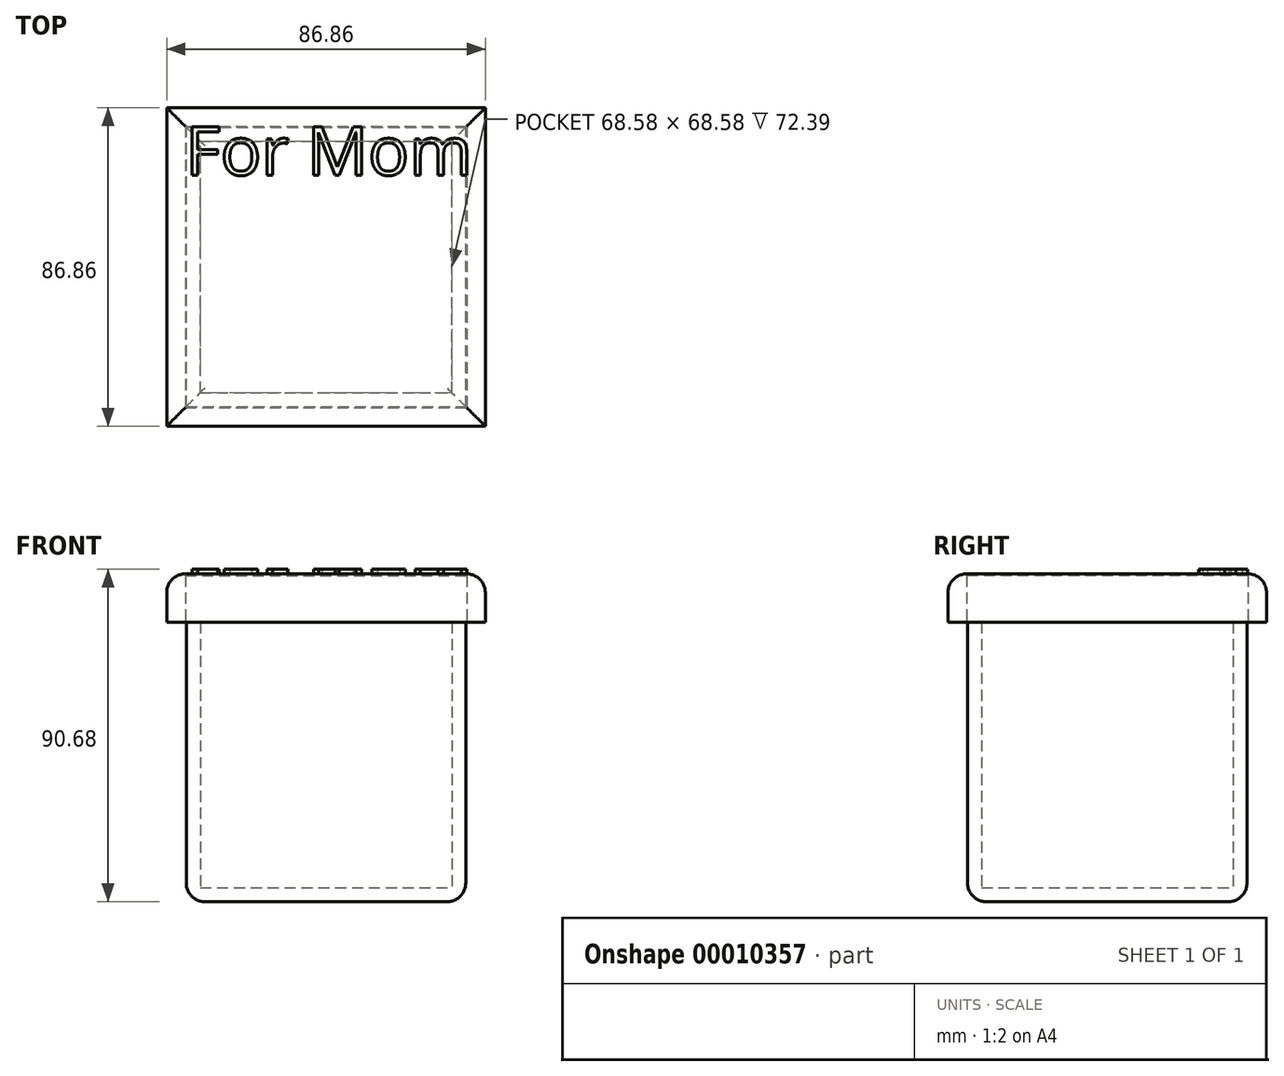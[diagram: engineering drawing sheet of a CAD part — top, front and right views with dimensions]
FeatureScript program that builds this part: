
annotation { "Feature Type Name" : "Feature", "Feature Type Description" : "" }
export const myFeature = defineFeature(function(context is Context, id is Id, definition is map)
    precondition{}
    {
        {
            var Q0;
            Q0=qCreatedBy(makeId("Front.planeOp"),FACE);
            var sketch = newSketch(context, id + "F0", { "sketchPlane" : qUnion([Q0])});
            skLineSegment(sketch, "E0.bottom", {"start": v(-76.2, 0) * mm, "end": v(0, 0) * mm});
            skLineSegment(sketch, "E0.top", {"start": v(-76.2, -76.2) * mm, "end": v(0, -76.2) * mm});
            skLineSegment(sketch, "E0.left", {"start": v(-76.2, 0) * mm, "end": v(-76.2, -76.2) * mm});
            skLineSegment(sketch, "E0.right", {"start": v(0, 0) * mm, "end": v(0, -76.2) * mm});
            skSolve(sketch);
        }
        {
            var Q0;
            Q0=makeQuery(id+"F0.imprint","IMPRINT",FACE,{"disambiguationData":[TD([[makeQuery(id+"F0.imprint","IMPRINT",EDGE,{"derivedFrom":sQuery(id+"F0.wireOp",EDGE,"E0.bottom")}),-1.0]])]});
            extrude(context, id + "F1", {"entities" : qUnion([Q0]), "depth" : 76.2 * mm});
        }
        {
            var Q0;
            Q0=makeQuery(id+"F1.opExtrude","SWEPT_FACE",FACE,{"disambiguationData":[OSD([sQuery(id+"F0.wireOp",EDGE,"E0.bottom")])]});
            shell(context, id + "F2", {"entities" : qUnion([Q0]), "thickness" : 3.8 * mm});
        }
        {
            var Q0;
            Q0=qCreatedBy(makeId("Top.planeOp"),FACE);
            var sketch = newSketch(context, id + "F3", { "sketchPlane" : qUnion([Q0])});
            skLineSegment(sketch, "E1.bottom", {"start": v(-76.2, 0) * mm, "end": v(0, 0) * mm});
            skLineSegment(sketch, "E1.top", {"start": v(-76.2, -76.2) * mm, "end": v(0, -76.2) * mm});
            skLineSegment(sketch, "E1.left", {"start": v(-76.2, 0) * mm, "end": v(-76.2, -76.2) * mm});
            skLineSegment(sketch, "E1.right", {"start": v(0, 0) * mm, "end": v(0, -76.2) * mm});
            skLineSegment(sketch, "E2.0", {"start": v(-76.45, 0.25) * mm, "end": v(0.25, 0.25) * mm});
            skLineSegment(sketch, "E2.1", {"start": v(-76.45, 0.25) * mm, "end": v(-76.45, -76.45) * mm});
            skLineSegment(sketch, "E2.2", {"start": v(-76.45, -76.45) * mm, "end": v(0.25, -76.45) * mm});
            skLineSegment(sketch, "E2.3", {"start": v(0.25, 0.25) * mm, "end": v(0.25, -76.45) * mm});
            skLineSegment(sketch, "E3.0", {"start": v(-81.53, 5.33) * mm, "end": v(5.33, 5.33) * mm});
            skLineSegment(sketch, "E3.1", {"start": v(-81.53, 5.33) * mm, "end": v(-81.53, -81.53) * mm});
            skLineSegment(sketch, "E3.2", {"start": v(-81.53, -81.53) * mm, "end": v(5.33, -81.53) * mm});
            skLineSegment(sketch, "E3.3", {"start": v(5.33, 5.33) * mm, "end": v(5.33, -81.53) * mm});
            skSolve(sketch);
        }
        {
            var Q0;
            Q0=makeQuery(id+"F3.imprint","IMPRINT",FACE,{"disambiguationData":[TD([[makeQuery(id+"F3.imprint","IMPRINT",EDGE,{"derivedFrom":sQuery(id+"F3.wireOp",EDGE,"E2.0")}),1.0]])]});
            extrude(context, id + "F4", {"entities" : qUnion([Q0]), "depth" : 12.7 * mm});
        }
        {
            var Q0;
            Q0=makeQuery(id+"F4.opExtrude","CAP_FACE",FACE,{"disambiguationData":[OSD([sQuery(id+"F3.wireOp",EDGE,"E2.0"),sQuery(id+"F3.wireOp",EDGE,"E2.1"),sQuery(id+"F3.wireOp",EDGE,"E2.2"),sQuery(id+"F3.wireOp",EDGE,"E2.3"),sQuery(id+"F3.wireOp",EDGE,"E3.0"),sQuery(id+"F3.wireOp",EDGE,"E3.1"),sQuery(id+"F3.wireOp",EDGE,"E3.2"),sQuery(id+"F3.wireOp",EDGE,"E3.3")])],"isStart":false});
            var sketch = newSketch(context, id + "F5", { "sketchPlane" : qUnion([Q0])});
            skLineSegment(sketch, "E4.bottom", {"start": v(-81.53, 5.33) * mm, "end": v(5.33, 5.33) * mm});
            skLineSegment(sketch, "E4.top", {"start": v(-81.53, -81.53) * mm, "end": v(5.33, -81.53) * mm});
            skLineSegment(sketch, "E4.left", {"start": v(-81.53, 5.33) * mm, "end": v(-81.53, -81.53) * mm});
            skLineSegment(sketch, "E4.right", {"start": v(5.33, 5.33) * mm, "end": v(5.33, -81.53) * mm});
            skSolve(sketch);
        }
        {
            var Q0;
            Q0 = qSketchRegion(id + "F5", true);
            extrude(context, id + "F6", {"entities" : qUnion([Q0]), "operationType" : NewBodyOperationType.ADD, "depth" : 0.5 * mm});
        }
        {
            var Q0;
            Q0=makeQuery(id+"F6.opExtrude","CAP_EDGE",EDGE,{"disambiguationData":[OSD([sQuery(id+"F5.wireOp",EDGE,"E4.top")])],"isStart":false});
            var Q1;
            Q1=makeQuery(id+"F6.opExtrude","CAP_EDGE",EDGE,{"disambiguationData":[OSD([sQuery(id+"F5.wireOp",EDGE,"E4.left")])],"isStart":false});
            var Q2;
            Q2=makeQuery(id+"F6.opExtrude","CAP_EDGE",EDGE,{"disambiguationData":[OSD([sQuery(id+"F5.wireOp",EDGE,"E4.right")])],"isStart":false});
            var Q3;
            Q3=makeQuery(id+"F6.opExtrude","CAP_EDGE",EDGE,{"disambiguationData":[OSD([sQuery(id+"F5.wireOp",EDGE,"E4.bottom")])],"isStart":false});
            fillet(context, id + "F7", {"entities" : qUnion([Q0, Q1, Q2, Q3]), "radius" : 5.08 * mm, "tangentPropagation" : true, "allowEdgeOverflow" : false});
        }
        {
            var Q0;
            Q0=makeQuery(id+"F1.opExtrude","SWEPT_EDGE",EDGE,{"disambiguationData":[OSD([sQuery(id+"F0.wireOp",EDGE,"E0.top"),sQuery(id+"F0.wireOp",EDGE,"E0.left")])]});
            var Q1;
            Q1=makeQuery(id+"F1.opExtrude","CAP_EDGE",EDGE,{"disambiguationData":[OSD([sQuery(id+"F0.wireOp",EDGE,"E0.top")])],"isStart":false});
            var Q2;
            Q2=makeQuery(id+"F1.opExtrude","SWEPT_EDGE",EDGE,{"disambiguationData":[OSD([sQuery(id+"F0.wireOp",EDGE,"E0.top"),sQuery(id+"F0.wireOp",EDGE,"E0.right")])]});
            var Q3;
            Q3=makeQuery(id+"F1.opExtrude","CAP_EDGE",EDGE,{"disambiguationData":[OSD([sQuery(id+"F0.wireOp",EDGE,"E0.top")])],"isStart":true});
            fillet(context, id + "F8", {"entities" : qUnion([Q0, Q1, Q2, Q3]), "radius" : 5.08 * mm, "tangentPropagation" : true, "allowEdgeOverflow" : false});
        }
        {
            var Q0;
            Q0=makeQuery(id+"F6.opExtrude","CAP_FACE",FACE,{"disambiguationData":[OSD([sQuery(id+"F5.wireOp",EDGE,"E4.bottom"),sQuery(id+"F5.wireOp",EDGE,"E4.top"),sQuery(id+"F5.wireOp",EDGE,"E4.left"),sQuery(id+"F5.wireOp",EDGE,"E4.right")])],"isStart":false});
            var sketch = newSketch(context, id + "F9", { "sketchPlane" : qUnion([Q0])});
            skText(sketch, "E5", { "text": "For Mom", "fontName": "OpenSans-Regular.ttf"});
            const initialGuessF9  = {"E5": [-0.07645, -0.01307, 1, 0, 0.01333]};
            skSetInitialGuess(sketch, initialGuessF9);
            skSolve(sketch);
        }
        {
            var Q0;
            Q0=makeQuery(id+"F9.imprint","IMPRINT",FACE,{"disambiguationData":[TD([[makeQuery(id+"F9.imprint","IMPRINT",EDGE,{"derivedFrom":sQuery(id+"F9.wireOp",EDGE,"E5.sketch_text.stroke-0")}),-1.0]])]});
            var Q1;
            Q1=makeQuery(id+"F9.imprint","IMPRINT",FACE,{"disambiguationData":[TD([[makeQuery(id+"F9.imprint","IMPRINT",EDGE,{"derivedFrom":sQuery(id+"F9.wireOp",EDGE,"E5.sketch_text.stroke-10")}),-1.0]])]});
            var Q2;
            Q2=makeQuery(id+"F9.imprint","IMPRINT",FACE,{"disambiguationData":[TD([[makeQuery(id+"F9.imprint","IMPRINT",EDGE,{"derivedFrom":sQuery(id+"F9.wireOp",EDGE,"E5.sketch_text.stroke-27")}),-1.0]])]});
            var Q3;
            Q3=makeQuery(id+"F9.imprint","IMPRINT",FACE,{"disambiguationData":[TD([[makeQuery(id+"F9.imprint","IMPRINT",EDGE,{"derivedFrom":sQuery(id+"F9.wireOp",EDGE,"E5.sketch_text.stroke-40")}),-1.0]])]});
            var Q4;
            Q4=makeQuery(id+"F9.imprint","IMPRINT",FACE,{"disambiguationData":[TD([[makeQuery(id+"F9.imprint","IMPRINT",EDGE,{"derivedFrom":sQuery(id+"F9.wireOp",EDGE,"E5.sketch_text.stroke-58")}),-1.0]])]});
            var Q5;
            Q5=makeQuery(id+"F9.imprint","IMPRINT",FACE,{"disambiguationData":[TD([[makeQuery(id+"F9.imprint","IMPRINT",EDGE,{"derivedFrom":sQuery(id+"F9.wireOp",EDGE,"E5.sketch_text.stroke-75")}),-1.0]])]});
            extrude(context, id + "F10", {"entities" : qUnion([Q0, Q1, Q2, Q3, Q4, Q5]), "operationType" : NewBodyOperationType.ADD, "depth" : 1.27 * mm});
        }
    });
